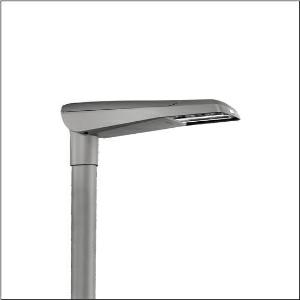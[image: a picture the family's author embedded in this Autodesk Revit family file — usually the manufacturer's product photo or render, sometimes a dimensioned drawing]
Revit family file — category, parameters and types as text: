
# Revit family: streetlight_sl_11_iq_micro___st1_2a_5xc1ac1g08ce_7479
name_source: partatom
category: Lighting Fixtures
units: mm (PartAtom-declared; Revit-internal decimal feet)

## family parameters
Cut with Voids When Loaded = No
Host = Face
Light Source = No
Part Type = Normal
Room Calculation Point = No
Round Connector Dimension = Use Diameter
Shared = No

## types (1)
- --- (1 x LED, 1600 lm, 14 W, 2200K)
    Apparent Load = 14 VA
    CIE Flux Codes = 33 71 96 100 100
    Color Rendering = 70
    Color Temperature = 2200K
    Default Elevation = 1800 mm
    Description = Streetlight SL 11 iQ micro, mast luminaire, primary light control with 3 zone facetted reflector, of plastic, silver coated, highly specular, primary optical cover: cover, of PMMA, transparent, light distribution: ST1.2a, light emission: direct distribution, primary light characteristic: asymmetric, installation type: post-top, side-entry, lamps: LED, High Power LED, rated values: 1.880lm | 13,8W | 136,2lm/W (begin service life); end service life: 1.880lm | 14W; at 50% lumin. flux: 940lm | 7,5W | 125,3lm/W, colour temperature: 2200/2700/3000/4000K, colour rendering: CRI > 70, light colour: 722/727/730/740, light setting 1 begin service life: 100% | 1.880lm | 13,8W | 136,2lm/W | 3.000K, light setting 1 end service life: 14W, further light settings possible, control: pre-setting: linear dimming characteristic, Street-Remote, Auto-Match, Temp-Guard, Lumen-Switch, Night-Set, Smart-Wire, Light-Fading, Desk-Remote (wireless, voltage-free reading and setting of iQ features in the workshop via application-optimized NFC function/RFID function), optimised constant luminous flux control (CLO 2.0), with cable H07RN-F 5x 1.5mm², mains connection: 220..240V, AC, 50/60Hz, connection cable pre-assembled, cable length: 5,5m, luminaire housing, of diecast aluminium, powder-coated, SITECO metallic grey (DB 702S), please order mast flange separately, inclination adjustable without tools: 0°, 5°, 10°, 15° (post-top) | 0°, -5°, -10°, -15° (side-entry), sealing non-destructively replaceable, multi-level sealing system, length: 600mm, width: 174mm, height: 116mm, mast flange for spigot size: 42mm (side-entry): 5XC10008XM4, 60/48mm (side-entry/post-top): 5XC10108XM2, 76/60mm (side-entry/post-top): 5XC10108XM1, equipment: standard, protection rating (complete): IP66, insulation class (complete): insulation class II (safety insulation), certification: CE, ENEC, ENEC+, VDE, impact resistance: IK10, permissible operating ambient temperature for outdoor applications: -25..+50°C, standard-compliant lighting for roads and squares, Environmental Product Declaration (EPD) tested and certified by an independent institute, packaging unit: 1 piece

Light Distribution: ST1.2a
    Height = 116 mm
    Lamp = 1 x LED
    Lamp Light Flux = 1600 lm
    Lamp Power = 14 W
    Lamp count = 1
    Length = 600 mm
    Luminous efficacy = 114 lm/W
    Manufacturer = Siteco
    ModVariant = No
    Model = 5XC1AC1G08CE
    Mounting Place = Pole
    Mounting Type = Pole top
    Number of Poles = 1
    OnlyDefault = Yes
    Power Factor = 1
    Product Name = Streetlight SL 11 iQ micro | ST1.2a
    Product group = mast luminaire | pylon top
    ProductGroupID = 6100
    Protection Class = Protection class II
    Protection Degree = IP 66
    RLX_Detail_Level = 1
    RLX_Emergency_Light_Flux = 0 lm
    RLX_Emergency_Type = 0
    RLX_Emergency_Type_DB = No
    RlxData = <blob elided: 58421 chars, md5=8e7112fc>
    Socket = socket
    Standby Power = 0 W
    System Light Flux = 1600 lm
    System Power = 14 W
    Type Comments = individual setting: luminous flux: 100 % | dim-lin: 254 | 369 mA
    Type Image = l_1006566.jpg
    URL = http://relux.com
    VarID = @adj_043795
    Voltage = 0 V
    Weight = 0.00 kg
    Width = 174 mm

## geometry (parser evidence)
native form markers: Blend x4, Sweep x10
no freeform markers — native parametric forms only
